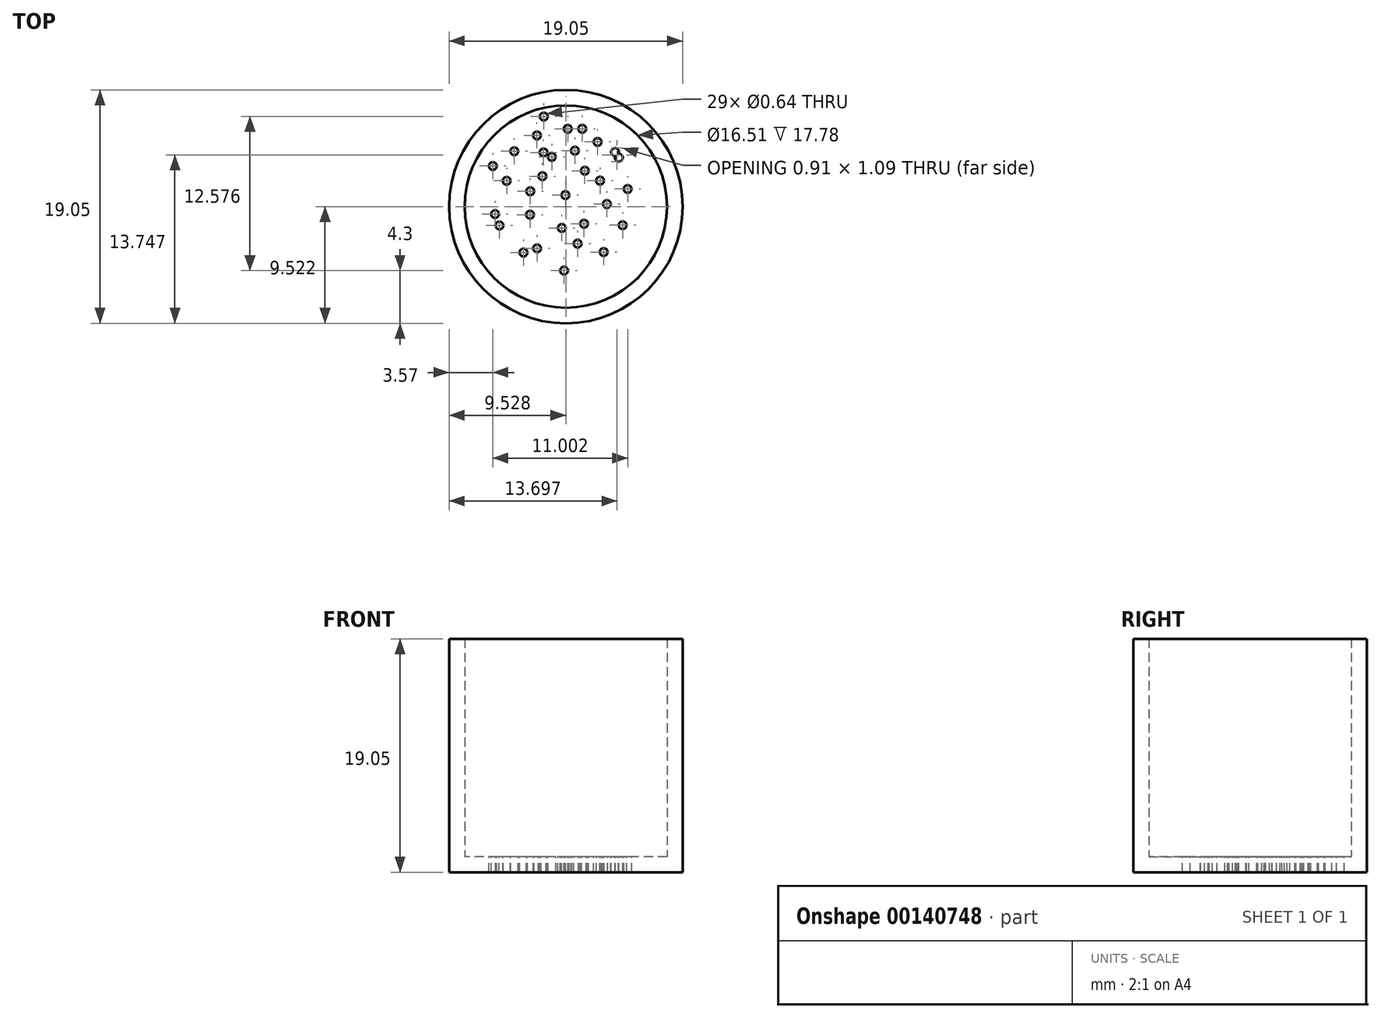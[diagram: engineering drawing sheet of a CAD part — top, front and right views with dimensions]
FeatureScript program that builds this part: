
annotation { "Feature Type Name" : "Feature", "Feature Type Description" : "" }
export const myFeature = defineFeature(function(context is Context, id is Id, definition is map)
    precondition{}
    {
        {
            var Q0;
            Q0=qCreatedBy(makeId("Top.planeOp"),FACE);
            var sketch = newSketch(context, id + "F0", { "sketchPlane" : qUnion([Q0])});
            skCircle(sketch, "E0", {"center": v(-115.14, 52.62) * mm, "radius": 9.53 * mm});
            skPoint(sketch, "E1", {"position": v(-119.18, 46.25) * mm});
            skPoint(sketch, "E2", {"position": v(-115.98, 46.21) * mm});
            skPoint(sketch, "E3", {"position": v(-112.38, 46.17) * mm});
            skPoint(sketch, "E4", {"position": v(-118.93, 49.23) * mm});
            skPoint(sketch, "E5", {"position": v(-115.52, 49.4) * mm});
            skPoint(sketch, "E6", {"position": v(-111.92, 49.35) * mm});
            skPoint(sketch, "E7", {"position": v(-122.32, 49.23) * mm});
            skPoint(sketch, "E8", {"position": v(-108.32, 49.35) * mm});
            skPoint(sketch, "E9", {"position": v(-122.68, 52.27) * mm});
            skPoint(sketch, "E10", {"position": v(-118.87, 52.42) * mm});
            skPoint(sketch, "E11", {"position": v(-112.07, 52.54) * mm});
            skPoint(sketch, "E12", {"position": v(-108.26, 52.9) * mm});
            skPoint(sketch, "E13", {"position": v(-108.26, 56.28) * mm});
            skPoint(sketch, "E14", {"position": v(-111.41, 56.28) * mm});
            skPoint(sketch, "E15", {"position": v(-114.82, 55.76) * mm});
            skPoint(sketch, "E16", {"position": v(-118.22, 55.8) * mm});
            skPoint(sketch, "E17", {"position": v(-121.62, 55.84) * mm});
            skPoint(sketch, "E18", {"position": v(-117.76, 58.98) * mm});
            skPoint(sketch, "E19", {"position": v(-114.96, 58.95) * mm});
            skPoint(sketch, "E20", {"position": v(-111.56, 58.9) * mm});
            skSolve(sketch);
        }
        {
            var Q0;
            Q0 = qSketchRegion(id + "F0", true);
            var Q1;
            Q1=sQuery(id+"F0.wireOp",EDGE,"E0");
            extrude(context, id + "F1", {"entities" : qUnion([Q0]), "surfaceEntities" : qUnion([Q1]), "depth" : 19.05 * mm});
        }
        {
            var Q0;
            Q0=makeQuery(id+"F1.opExtrude","CAP_FACE",FACE,{"disambiguationData":[OSD([sQuery(id+"F0.wireOp",EDGE,"E0")])],"isStart":false});
            shell(context, id + "F2", {"entities" : qUnion([Q0]), "thickness" : 1.27 * mm});
        }
        {
            var Q0;
            {var subQ0=sQuery(id+"F0.wireOp",EDGE,"E0");Q0=makeQuery(id+"F2.opShell","OFFSET_FACE",FACE,{"disambiguationData":[OSD([subQ0]),TDD([makeQuery(id+"F1.opExtrude","CAP_FACE",FACE,{"disambiguationData":[OSD([subQ0])],"isStart":true})])]});}
            var sketch = newSketch(context, id + "F3", { "sketchPlane" : qUnion([Q0])});
            skPoint(sketch, "E21", {"position": v(-116.94, 59.98) * mm});
            skPoint(sketch, "E22", {"position": v(-113.8, 58.97) * mm});
            skPoint(sketch, "E23", {"position": v(-114.99, 58.97) * mm});
            skPoint(sketch, "E24", {"position": v(-112.55, 57.9) * mm});
            skPoint(sketch, "E25", {"position": v(-111.13, 57.08) * mm});
            skPoint(sketch, "E26", {"position": v(-110.82, 56.62) * mm});
            skPoint(sketch, "E27", {"position": v(-116.3, 56.68) * mm});
            skPoint(sketch, "E28", {"position": v(-116.96, 57.04) * mm});
            skPoint(sketch, "E29", {"position": v(-111.8, 52.83) * mm});
            skPoint(sketch, "E30", {"position": v(-118.06, 51.96) * mm});
            skPoint(sketch, "E31", {"position": v(-119.97, 54.73) * mm});
            skPoint(sketch, "E32", {"position": v(-114.19, 49.6) * mm});
            skPoint(sketch, "E33", {"position": v(-115.18, 53.56) * mm});
            skPoint(sketch, "E34", {"position": v(-120.56, 51.08) * mm});
            skPoint(sketch, "E35", {"position": v(-120.92, 52.01) * mm});
            skPoint(sketch, "E36", {"position": v(-118.05, 53.87) * mm});
            skPoint(sketch, "E37", {"position": v(-119.35, 57.14) * mm});
            skPoint(sketch, "E38", {"position": v(-113.6, 55.55) * mm});
            skPoint(sketch, "E39", {"position": v(-110.1, 54.06) * mm});
            skPoint(sketch, "E40", {"position": v(-110.51, 51.1) * mm});
            skPoint(sketch, "E41", {"position": v(-109.94, 54.12) * mm});
            skPoint(sketch, "E42", {"position": v(-115.47, 50.88) * mm});
            skPoint(sketch, "E43", {"position": v(-117.5, 49.2) * mm});
            skPoint(sketch, "E44", {"position": v(-118.6, 48.87) * mm});
            skPoint(sketch, "E45", {"position": v(-112.06, 48.91) * mm});
            skPoint(sketch, "E46", {"position": v(-113.66, 51.22) * mm});
            skPoint(sketch, "E47", {"position": v(-112.35, 54.74) * mm});
            skPoint(sketch, "E48", {"position": v(-117.06, 55.1) * mm});
            skPoint(sketch, "E49", {"position": v(-121.1, 55.93) * mm});
            skPoint(sketch, "E50", {"position": v(-115.29, 47.4) * mm});
            skPoint(sketch, "E51", {"position": v(-114.4, 57.19) * mm});
            skPoint(sketch, "E52", {"position": v(-117.5, 58.43) * mm});
            skSolve(sketch);
        }
        {
            var Q0;
            Q0=sQuery(id+"F3.wireOp",VERTEX,"E21");
            var Q1;
            Q1=sQuery(id+"F3.wireOp",VERTEX,"E23");
            var Q2;
            Q2=sQuery(id+"F3.wireOp",VERTEX,"E22");
            var Q3;
            Q3=sQuery(id+"F3.wireOp",VERTEX,"E52");
            var Q4;
            Q4=sQuery(id+"F3.wireOp",VERTEX,"E37");
            var Q5;
            Q5=sQuery(id+"F3.wireOp",VERTEX,"E49");
            var Q6;
            Q6=sQuery(id+"F3.wireOp",VERTEX,"E31");
            var Q7;
            Q7=sQuery(id+"F3.wireOp",VERTEX,"E28");
            var Q8;
            Q8=sQuery(id+"F3.wireOp",VERTEX,"E27");
            var Q9;
            Q9=sQuery(id+"F3.wireOp",VERTEX,"E48");
            var Q10;
            Q10=sQuery(id+"F3.wireOp",VERTEX,"E36");
            var Q11;
            Q11=sQuery(id+"F3.wireOp",VERTEX,"E35");
            var Q12;
            Q12=sQuery(id+"F3.wireOp",VERTEX,"E34");
            var Q13;
            Q13=sQuery(id+"F3.wireOp",VERTEX,"E30");
            var Q14;
            Q14=sQuery(id+"F3.wireOp",VERTEX,"E44");
            var Q15;
            Q15=sQuery(id+"F3.wireOp",VERTEX,"E43");
            var Q16;
            Q16=sQuery(id+"F3.wireOp",VERTEX,"E42");
            var Q17;
            Q17=sQuery(id+"F3.wireOp",VERTEX,"E33");
            var Q18;
            Q18=sQuery(id+"F3.wireOp",VERTEX,"E51");
            var Q19;
            Q19=sQuery(id+"F3.wireOp",VERTEX,"E38");
            var Q20;
            Q20=sQuery(id+"F3.wireOp",VERTEX,"E25");
            var Q21;
            Q21=sQuery(id+"F3.wireOp",VERTEX,"E26");
            var Q22;
            Q22=sQuery(id+"F3.wireOp",VERTEX,"E47");
            var Q23;
            Q23=sQuery(id+"F3.wireOp",VERTEX,"E29");
            var Q24;
            Q24=sQuery(id+"F3.wireOp",VERTEX,"E39");
            var Q25;
            Q25=sQuery(id+"F3.wireOp",VERTEX,"E40");
            var Q26;
            Q26=sQuery(id+"F3.wireOp",VERTEX,"E46");
            var Q27;
            Q27=sQuery(id+"F3.wireOp",VERTEX,"E32");
            var Q28;
            Q28=sQuery(id+"F3.wireOp",VERTEX,"E45");
            var Q29;
            Q29=sQuery(id+"F3.wireOp",VERTEX,"E50");
            var Q30;
            Q30=sQuery(id+"F3.wireOp",VERTEX,"E24");
            var Q31;
            Q31=makeQuery(id+"F1.opExtrude","SWEPT_BODY",BODY,{"disambiguationData":[OSD([sQuery(id+"F0.wireOp",EDGE,"E0")])]});
            hole(context, id + "F4", {"style" : HoleStyle.SIMPLE, "endStyle" : HoleEndStyle.THROUGH, "holeDiameter" : 0.64 * mm, "locations" : qUnion([Q0, Q1, Q2, Q3, Q4, Q5, Q6, Q7, Q8, Q9, Q10, Q11, Q12, Q13, Q14, Q15, Q16, Q17, Q18, Q19, Q20, Q21, Q22, Q23, Q24, Q25, Q26, Q27, Q28, Q29, Q30]), "scope" : qUnion([Q31]), "isTappedThrough" : true});
        }
        {
            var Q0;
            Q0=qCreatedBy(makeId("Right.planeOp"),FACE);
            var sketch = newSketch(context, id + "F5", { "sketchPlane" : qUnion([Q0])});
            skCircle(sketch, "E53", {"center": v(52.85, 10.37) * mm, "radius": 4.1 * mm});
            skSolve(sketch);
        }
        {
            var Q0;
            Q0=sQuery(id+"F5.wireOp",EDGE,"E53");
            extrude(context, id + "F6", {"bodyType" : ToolBodyType.SURFACE, "surfaceEntities" : qUnion([Q0]), "oppositeDirection" : true, "depth" : 106.76 * mm});
        }
    });
